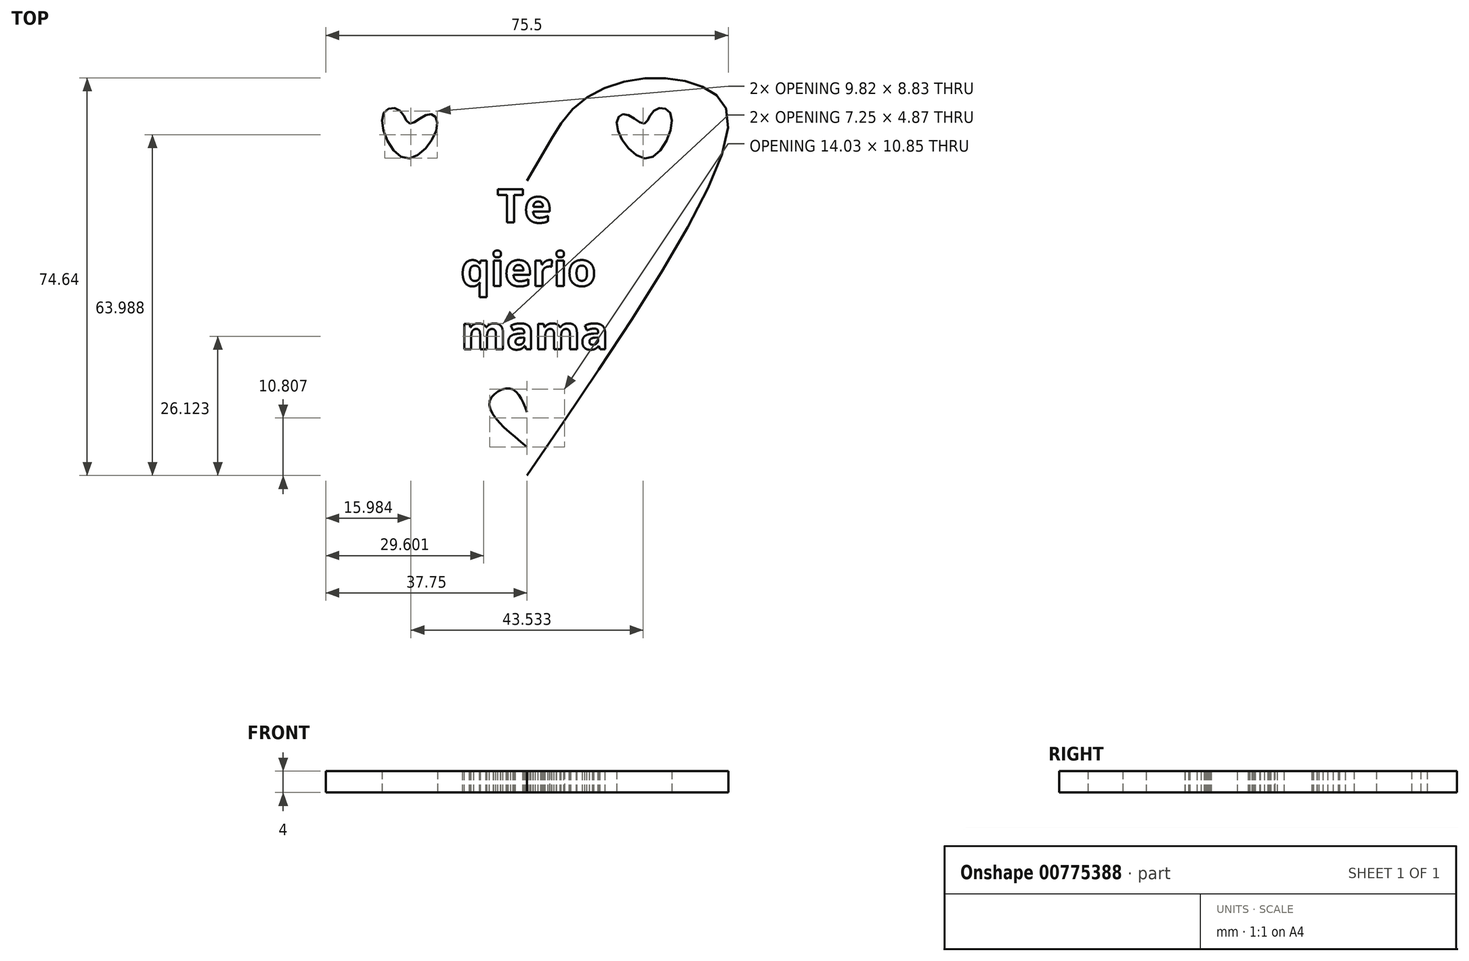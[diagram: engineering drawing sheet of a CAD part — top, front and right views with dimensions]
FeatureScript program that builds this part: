
annotation { "Feature Type Name" : "Feature", "Feature Type Description" : "" }
export const myFeature = defineFeature(function(context is Context, id is Id, definition is map)
    precondition{}
    {
        {
            var Q0;
            Q0=qCreatedBy(makeId("Top.planeOp"),FACE);
            var sketch = newSketch(context, id + "F0", { "sketchPlane" : qUnion([Q0])});
            skFitSpline(sketch, "E0", {"points": [v(0, 1.54) * mm, v(4.13, 8.64) * mm, v(10.28, 16.52) * mm, v(22, 20.75) * mm, v(33.33, 19.02) * mm, v(37.75, 12.3) * mm, v(0, -53.79) * mm], "startDerivative": vector(34.2, 59.2) * mm, "endDerivative": vector(-158.14, -231.7) * mm});
            skFitSpline(sketch, "E1", {"points": [v(22, 12.3) * mm, v(23.92, 14.8) * mm, v(27, 14.02) * mm, v(22.76, 5.76) * mm, v(16.8, 12.1) * mm, v(18.54, 14.02) * mm, v(22, 12.3) * mm]});
            skFitSpline(sketch, "E2", {"points": [v(0, -41.88) * mm, v(3.17, -37.46) * mm, v(7.01, -39.96) * mm, v(0, -48.4) * mm], "startDerivative": vector(8.02, 20.7) * mm, "endDerivative": vector(-26.44, -21.48) * mm});
            skFitSpline(sketch, "E3.MirrorCS", {"points": [v(0, 1.54) * mm, v(-4.13, 8.64) * mm, v(-10.28, 16.52) * mm, v(-22, 20.75) * mm, v(-33.33, 19.02) * mm, v(-37.75, 12.3) * mm, v(0, -53.79) * mm], "startDerivative": vector(-34.2, 59.2) * mm, "endDerivative": vector(158.14, -231.7) * mm});
            skFitSpline(sketch, "E4.MirrorCS", {"points": [v(0, -41.88) * mm, v(-3.17, -37.46) * mm, v(-7.01, -39.96) * mm, v(0, -48.4) * mm], "startDerivative": vector(-8.02, 20.7) * mm, "endDerivative": vector(26.44, -21.48) * mm});
            skFitSpline(sketch, "E5.MirrorC", {"points": [v(-22, 12.3) * mm, v(-23.92, 14.8) * mm, v(-27, 14.02) * mm, v(-22.76, 5.76) * mm, v(-16.8, 12.1) * mm, v(-18.54, 14.02) * mm, v(-22, 12.3) * mm]});
            skSolve(sketch);
        }
        {
            var Q0;
            Q0=makeQuery(id+"F0.imprint","IMPRINT",FACE,{"disambiguationData":[TD([[makeQuery(id+"F0.imprint","IMPRINT",EDGE,{"derivedFrom":sQuery(id+"F0.wireOp",EDGE,"E0")}),-1.0]])]});
            extrude(context, id + "F1", {"entities" : qUnion([Q0]), "depth" : 4 * mm, "offsetDistance" : 25 * mm});
        }
        {
            var Q0;
            Q0=makeQuery(id+"F1.opExtrude","CAP_FACE",FACE,{"disambiguationData":[OSD([sQuery(id+"F0.wireOp",EDGE,"E0"),sQuery(id+"F0.wireOp",EDGE,"E1"),sQuery(id+"F0.wireOp",EDGE,"E2"),sQuery(id+"F0.wireOp",EDGE,"E3.MirrorCS"),sQuery(id+"F0.wireOp",EDGE,"E4.MirrorCS"),sQuery(id+"F0.wireOp",EDGE,"E5.MirrorC")])],"isStart":false});
            var sketch = newSketch(context, id + "F2", { "sketchPlane" : qUnion([Q0])});
            skText(sketch, "E6", { "text": "   Te\nqierio\nmama", "fontName": "OpenSans-Bold.ttf"});
            const initialGuessF2  = {"E6": [-0.01246, -0.0063, 1, 0, 0.0063]};
            skSetInitialGuess(sketch, initialGuessF2);
            skSolve(sketch);
        }
        {
            var Q0;
            Q0 = qSketchRegion(id + "F2", true);
            extrude(context, id + "F3", {"entities" : qUnion([Q0]), "operationType" : NewBodyOperationType.REMOVE, "oppositeDirection" : true, "depth" : 25 * mm, "offsetDistance" : 25 * mm});
        }
    });
